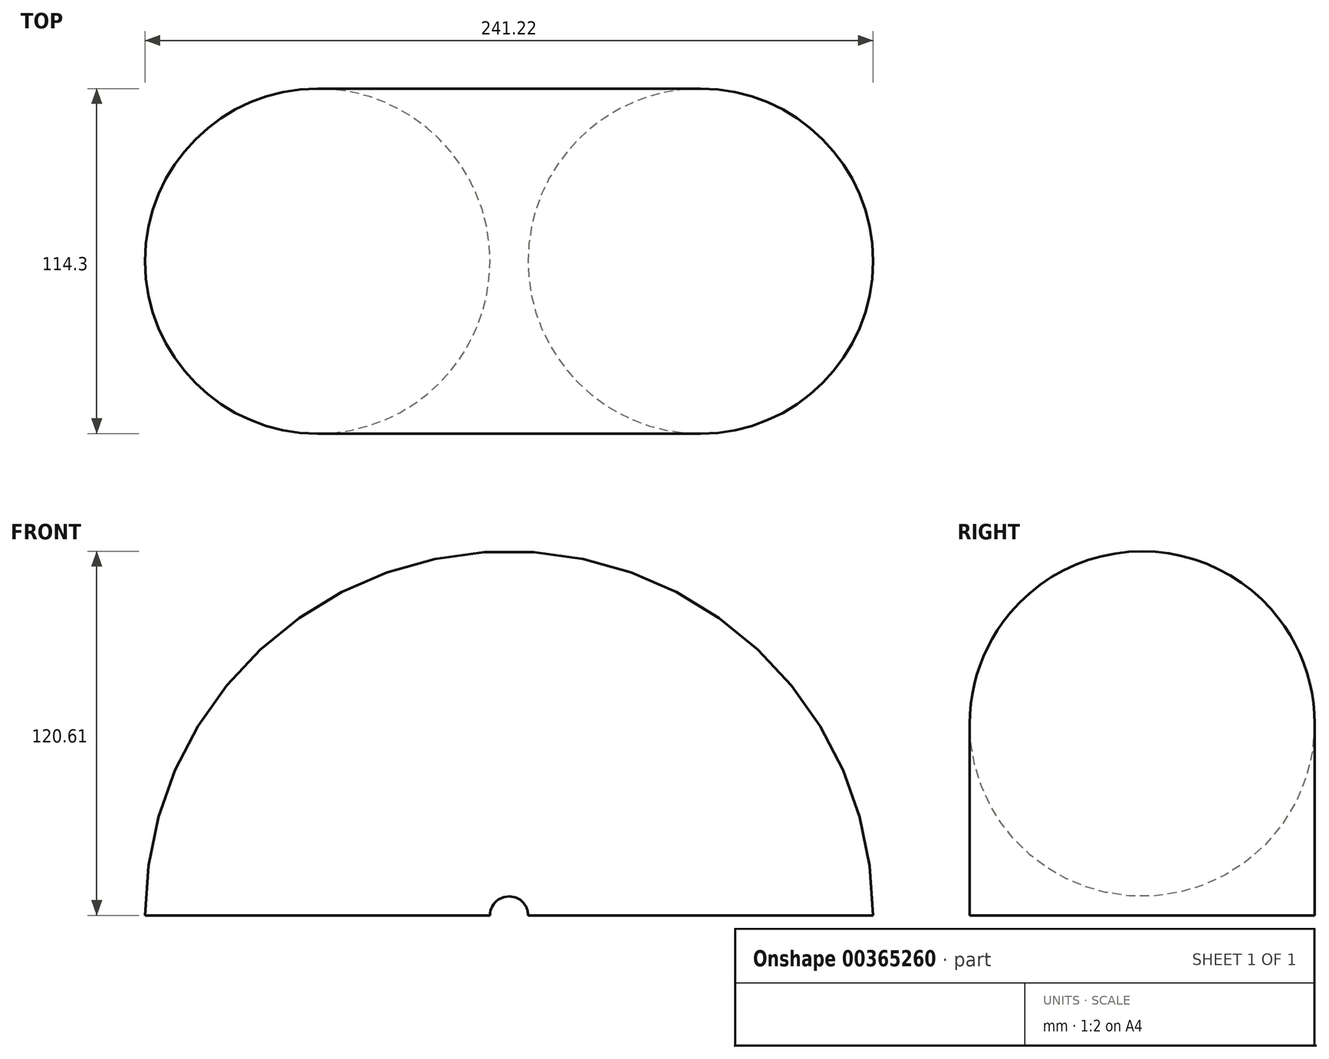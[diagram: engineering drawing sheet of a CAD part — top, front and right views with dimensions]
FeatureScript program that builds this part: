
annotation { "Feature Type Name" : "Feature", "Feature Type Description" : "" }
export const myFeature = defineFeature(function(context is Context, id is Id, definition is map)
    precondition{}
    {
        {
            var Q0;
            Q0=qCreatedBy(makeId("Front.planeOp"),FACE);
            var sketch = newSketch(context, id + "F0", { "sketchPlane" : qUnion([Q0])});
            skArc(sketch, "E0", {"start": v(87, 0) * mm, "mid": v(23.5, 63.5) * mm, "end": v(-40, 0) * mm});
            skSolve(sketch);
        }
        {
            var Q0;
            Q0=sQuery(id+"F0.wireOp",VERTEX,"E0.start");
            var Q1;
            Q1=sQuery(id+"F0.wireOp",EDGE,"E0");
            cPlane(context, id + "F1", {"entities" : qUnion([Q0, Q1]), "cplaneType" : CPlaneType.CURVE_POINT, "offset" : 25.4 * mm, "width" : 152.4 * mm, "height" : 152.4 * mm});
        }
        {
            var Q0;
            Q0=qCreatedBy(id+"F1.planeOp",FACE);
            var sketch = newSketch(context, id + "F2", { "sketchPlane" : qUnion([Q0])});
            skCircle(sketch, "E1", {"center": v(86.97, -0.01) * mm, "radius": 57.15 * mm});
            skSolve(sketch);
        }
        {
            var Q0;
            Q0=makeQuery(id+"F2.imprint","IMPRINT",FACE,{"disambiguationData":[TD([[makeQuery(id+"F2.imprint","IMPRINT",EDGE,{"derivedFrom":sQuery(id+"F2.wireOp",EDGE,"E1")}),1.0]])]});
            var Q1;
            Q1=qConstructionFilter(qBodyType(qCreatedBy(id+"F0",EDGE),BodyType.WIRE),ConstructionObject.NO);
            sweep(context, id + "F3", {"profiles" : qUnion([Q0]), "path" : qUnion([Q1])});
        }
    });
